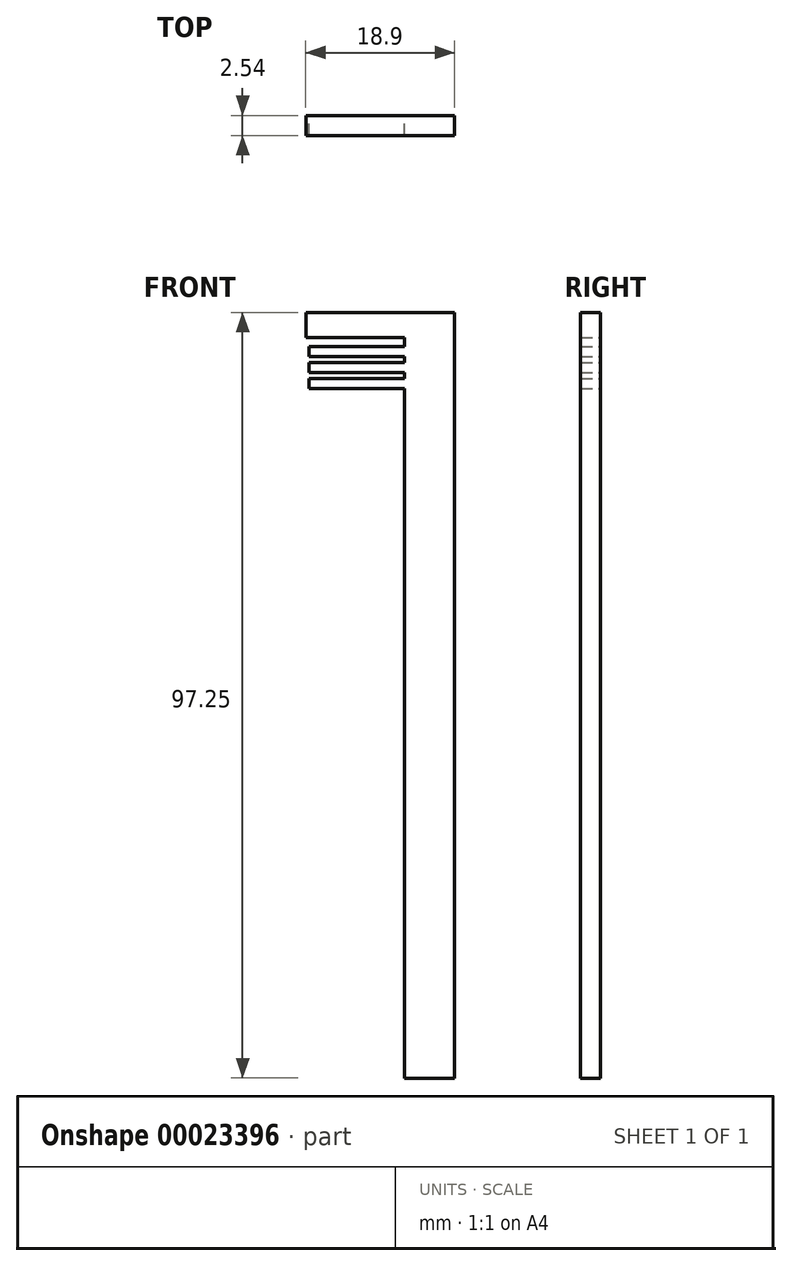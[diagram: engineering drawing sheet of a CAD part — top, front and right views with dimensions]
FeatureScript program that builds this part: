
annotation { "Feature Type Name" : "Feature", "Feature Type Description" : "" }
export const myFeature = defineFeature(function(context is Context, id is Id, definition is map)
    precondition{}
    {
        {
            var Q0;
            Q0=qCreatedBy(makeId("Front.planeOp"),FACE);
            var sketch = newSketch(context, id + "F0", { "sketchPlane" : qUnion([Q0])});
            skLineSegment(sketch, "E0.top", {"start": v(-6.35, 54.6) * mm, "end": v(-18.9, 54.6) * mm});
            skLineSegment(sketch, "E0.right", {"start": v(-18.9, 57.8) * mm, "end": v(-18.9, 54.6) * mm});
            skLineSegment(sketch, "E1", {"start": v(-6.35, 54.6) * mm, "end": v(-6.35, 53.45) * mm});
            skLineSegment(sketch, "E2", {"start": v(-6.35, -39.46) * mm, "end": v(0, -39.46) * mm});
            skLineSegment(sketch, "E3", {"start": v(0, 57.8) * mm, "end": v(0, -39.46) * mm});
            skLineSegment(sketch, "E4", {"start": v(-6.35, 53.45) * mm, "end": v(-18.48, 53.45) * mm});
            skLineSegment(sketch, "E5", {"start": v(-18.48, 53.45) * mm, "end": v(-18.48, 52.18) * mm});
            skLineSegment(sketch, "E6", {"start": v(-18.48, 52.18) * mm, "end": v(-6.35, 52.18) * mm});
            skLineSegment(sketch, "E7", {"start": v(-18.9, 57.8) * mm, "end": v(0, 57.8) * mm});
            skPoint(sketch, "E8.orphan", {"position": v(-18.9, 60.98) * mm});
            skLineSegment(sketch, "E9", {"start": v(-6.35, 51.42) * mm, "end": v(-18.48, 51.42) * mm});
            skLineSegment(sketch, "E10", {"start": v(-18.48, 51.42) * mm, "end": v(-18.48, 50.15) * mm});
            skLineSegment(sketch, "E11", {"start": v(-18.48, 50.15) * mm, "end": v(-6.35, 50.15) * mm});
            skLineSegment(sketch, "E12", {"start": v(-6.35, 49.39) * mm, "end": v(-18.48, 49.39) * mm});
            skLineSegment(sketch, "E13", {"start": v(-18.48, 49.39) * mm, "end": v(-18.48, 48.12) * mm});
            skLineSegment(sketch, "E14", {"start": v(-18.48, 48.12) * mm, "end": v(-6.35, 48.12) * mm});
            skLineSegment(sketch, "E15.trimOffspring", {"start": v(-6.35, 50.15) * mm, "end": v(-6.35, 49.39) * mm});
            skLineSegment(sketch, "E16.trimOffspring", {"start": v(-6.35, 48.12) * mm, "end": v(-6.35, -39.46) * mm});
            skLineSegment(sketch, "E17", {"start": v(-6.35, 52.18) * mm, "end": v(-6.35, 51.42) * mm});
            skLineSegment(sketch, "E18", {"start": v(-6.35, 48.12) * mm, "end": v(-6.35, 47.36) * mm});
            skLineSegment(sketch, "E19", {"start": v(-6.35, 47.36) * mm, "end": v(-6.35, 46.09) * mm});
            skLineSegment(sketch, "E20", {"start": v(-6.35, 46.09) * mm, "end": v(-6.35, 45.32) * mm});
            skLineSegment(sketch, "E21", {"start": v(-6.35, 45.32) * mm, "end": v(-6.35, 44.05) * mm});
            skLineSegment(sketch, "E22", {"start": v(-6.35, 44.05) * mm, "end": v(-6.35, 43.3) * mm});
            skLineSegment(sketch, "E23", {"start": v(-6.35, 43.3) * mm, "end": v(-6.35, 42.02) * mm});
            skLineSegment(sketch, "E24", {"start": v(-6.35, 42.02) * mm, "end": v(-6.35, 41.26) * mm});
            skLineSegment(sketch, "E25", {"start": v(-6.35, 41.26) * mm, "end": v(-6.35, 39.99) * mm});
            skLineSegment(sketch, "E26", {"start": v(-6.35, 39.99) * mm, "end": v(-6.35, 39.23) * mm});
            skLineSegment(sketch, "E27", {"start": v(-6.35, 39.23) * mm, "end": v(-6.35, 37.96) * mm});
            skLineSegment(sketch, "E28", {"start": v(-6.35, 37.96) * mm, "end": v(-6.35, 37.2) * mm});
            skLineSegment(sketch, "E29", {"start": v(-6.35, 37.2) * mm, "end": v(-6.35, 35.93) * mm});
            skLineSegment(sketch, "E30", {"start": v(-6.35, 35.93) * mm, "end": v(-6.35, 35.16) * mm});
            skLineSegment(sketch, "E31", {"start": v(-6.35, 35.16) * mm, "end": v(-6.35, 33.9) * mm});
            skLineSegment(sketch, "E32", {"start": v(-6.35, 33.9) * mm, "end": v(-6.35, 33.13) * mm});
            skLineSegment(sketch, "E33", {"start": v(-6.35, 33.13) * mm, "end": v(-6.35, 31.86) * mm});
            skLineSegment(sketch, "E34", {"start": v(-6.35, 31.86) * mm, "end": v(-6.35, 31.1) * mm});
            skLineSegment(sketch, "E35", {"start": v(-6.35, 31.1) * mm, "end": v(-6.35, 29.83) * mm});
            skLineSegment(sketch, "E36", {"start": v(-6.35, 29.83) * mm, "end": v(-6.35, 29.07) * mm});
            skLineSegment(sketch, "E37", {"start": v(-6.35, 29.07) * mm, "end": v(-6.35, 27.8) * mm});
            skLineSegment(sketch, "E38", {"start": v(-6.35, 27.8) * mm, "end": v(-6.35, 27.04) * mm});
            skLineSegment(sketch, "E39", {"start": v(-6.35, 47.36) * mm, "end": v(-18.48, 47.36) * mm});
            skLineSegment(sketch, "E40", {"start": v(-18.48, 47.36) * mm, "end": v(-18.48, 46.09) * mm});
            skLineSegment(sketch, "E41", {"start": v(-18.48, 46.09) * mm, "end": v(-6.35, 46.09) * mm});
            skLineSegment(sketch, "E42", {"start": v(-6.35, 45.32) * mm, "end": v(-18.48, 45.32) * mm});
            skLineSegment(sketch, "E43", {"start": v(-18.48, 45.32) * mm, "end": v(-18.48, 44.05) * mm});
            skLineSegment(sketch, "E44", {"start": v(-18.48, 44.05) * mm, "end": v(-6.35, 44.05) * mm});
            skLineSegment(sketch, "E45", {"start": v(-6.35, 43.3) * mm, "end": v(-18.48, 43.3) * mm});
            skLineSegment(sketch, "E46", {"start": v(-18.48, 43.3) * mm, "end": v(-18.48, 42.02) * mm});
            skLineSegment(sketch, "E47", {"start": v(-18.48, 42.02) * mm, "end": v(-6.35, 42.02) * mm});
            skLineSegment(sketch, "E48", {"start": v(-6.35, 41.26) * mm, "end": v(-18.48, 41.26) * mm});
            skLineSegment(sketch, "E49", {"start": v(-18.48, 41.26) * mm, "end": v(-18.48, 39.99) * mm});
            skLineSegment(sketch, "E50", {"start": v(-18.48, 39.99) * mm, "end": v(-6.35, 39.99) * mm});
            skLineSegment(sketch, "E51", {"start": v(-6.35, 39.23) * mm, "end": v(-18.48, 39.23) * mm});
            skLineSegment(sketch, "E52", {"start": v(-18.48, 39.23) * mm, "end": v(-18.48, 37.96) * mm});
            skLineSegment(sketch, "E53", {"start": v(-18.48, 37.96) * mm, "end": v(-6.35, 37.96) * mm});
            skLineSegment(sketch, "E54", {"start": v(-6.35, 37.2) * mm, "end": v(-18.48, 37.2) * mm});
            skLineSegment(sketch, "E55", {"start": v(-18.48, 37.2) * mm, "end": v(-18.48, 35.93) * mm});
            skLineSegment(sketch, "E56", {"start": v(-18.48, 35.93) * mm, "end": v(-6.35, 35.93) * mm});
            skLineSegment(sketch, "E57", {"start": v(-18.48, 35.16) * mm, "end": v(-6.35, 35.16) * mm});
            skLineSegment(sketch, "E58", {"start": v(-6.35, 33.9) * mm, "end": v(-18.48, 33.9) * mm});
            skLineSegment(sketch, "E59", {"start": v(-18.48, 33.9) * mm, "end": v(-18.48, 35.16) * mm});
            skLineSegment(sketch, "E60", {"start": v(-6.35, 33.13) * mm, "end": v(-18.48, 33.13) * mm});
            skLineSegment(sketch, "E61", {"start": v(-18.48, 33.13) * mm, "end": v(-18.48, 31.86) * mm});
            skLineSegment(sketch, "E62", {"start": v(-18.48, 31.86) * mm, "end": v(-6.35, 31.86) * mm});
            skLineSegment(sketch, "E63", {"start": v(-6.35, 31.1) * mm, "end": v(-18.48, 31.1) * mm});
            skLineSegment(sketch, "E64", {"start": v(-18.48, 31.1) * mm, "end": v(-18.48, 29.83) * mm});
            skLineSegment(sketch, "E65", {"start": v(-18.48, 29.83) * mm, "end": v(-6.35, 29.83) * mm});
            skLineSegment(sketch, "E66", {"start": v(-6.35, 29.07) * mm, "end": v(-18.48, 29.07) * mm});
            skLineSegment(sketch, "E67", {"start": v(-18.48, 29.07) * mm, "end": v(-18.48, 27.8) * mm});
            skLineSegment(sketch, "E68", {"start": v(-18.48, 27.8) * mm, "end": v(-6.35, 27.8) * mm});
            skLineSegment(sketch, "E69", {"start": v(-6.35, 27.04) * mm, "end": v(-6.35, 25.77) * mm});
            skLineSegment(sketch, "E70", {"start": v(-6.35, 25.77) * mm, "end": v(-6.35, 25) * mm});
            skLineSegment(sketch, "E71", {"start": v(-6.35, 25) * mm, "end": v(-6.35, 23.73) * mm});
            skLineSegment(sketch, "E72", {"start": v(-6.35, 24.25) * mm, "end": v(-6.35, 23.73) * mm});
            skLineSegment(sketch, "E73", {"start": v(-6.35, 24.25) * mm, "end": v(-6.35, 22.97) * mm});
            skLineSegment(sketch, "E74", {"start": v(-6.35, 22.97) * mm, "end": v(-6.35, 21.7) * mm});
            skLineSegment(sketch, "E75", {"start": v(-6.35, 21.8) * mm, "end": v(-6.35, 21.7) * mm});
            skLineSegment(sketch, "E76", {"start": v(-6.35, 21.8) * mm, "end": v(-6.35, 20.94) * mm});
            skLineSegment(sketch, "E77", {"start": v(-6.35, 20.94) * mm, "end": v(-6.35, 19.67) * mm});
            skLineSegment(sketch, "E78", {"start": v(-6.35, 19.67) * mm, "end": v(-6.35, 18.9) * mm});
            skLineSegment(sketch, "E79", {"start": v(-6.35, 18.9) * mm, "end": v(-6.35, 17.64) * mm});
            skLineSegment(sketch, "E80", {"start": v(-6.35, 17.64) * mm, "end": v(-6.35, 16.88) * mm});
            skLineSegment(sketch, "E81", {"start": v(-6.35, 16.88) * mm, "end": v(-6.35, 15.6) * mm});
            skLineSegment(sketch, "E82", {"start": v(-6.35, 15.6) * mm, "end": v(-6.35, 14.84) * mm});
            skLineSegment(sketch, "E83", {"start": v(-6.35, 14.84) * mm, "end": v(-6.35, 13.57) * mm});
            skLineSegment(sketch, "E84", {"start": v(-6.35, 13.57) * mm, "end": v(-6.35, 12.81) * mm});
            skLineSegment(sketch, "E85", {"start": v(-6.35, 12.81) * mm, "end": v(-6.35, 10.85) * mm});
            skLineSegment(sketch, "E86", {"start": v(-6.35, 10.85) * mm, "end": v(-6.35, 9.73) * mm});
            skLineSegment(sketch, "E87", {"start": v(-6.35, 9.73) * mm, "end": v(-6.35, 8.79) * mm});
            skLineSegment(sketch, "E88", {"start": v(-6.35, 8.79) * mm, "end": v(-6.35, 7.94) * mm});
            skLineSegment(sketch, "E89", {"start": v(-6.35, 7.94) * mm, "end": v(-6.35, 6.92) * mm});
            skLineSegment(sketch, "E90", {"start": v(-6.35, 6.92) * mm, "end": v(-6.35, 5.67) * mm});
            skLineSegment(sketch, "E91", {"start": v(-6.35, 5.67) * mm, "end": v(-6.35, 4.33) * mm});
            skLineSegment(sketch, "E92", {"start": v(-6.35, 4.33) * mm, "end": v(-6.35, 2.9) * mm});
            skLineSegment(sketch, "E93", {"start": v(-6.35, 2.9) * mm, "end": v(-6.35, 1.65) * mm});
            skLineSegment(sketch, "E94", {"start": v(-6.35, 1.65) * mm, "end": v(-6.35, 0.58) * mm});
            skLineSegment(sketch, "E95", {"start": v(-6.35, 0.58) * mm, "end": v(-6.35, -0.67) * mm});
            skLineSegment(sketch, "E96", {"start": v(-6.35, -0.67) * mm, "end": v(-6.35, -1.91) * mm});
            skLineSegment(sketch, "E97", {"start": v(-6.35, -1.91) * mm, "end": v(-6.35, -3.38) * mm});
            skLineSegment(sketch, "E98", {"start": v(-6.35, -3.38) * mm, "end": v(-6.35, -4.85) * mm});
            skLineSegment(sketch, "E99", {"start": v(-6.35, -4.85) * mm, "end": v(-6.35, -5.53) * mm});
            skLineSegment(sketch, "E100", {"start": v(-6.35, -5.53) * mm, "end": v(-6.35, -7.36) * mm});
            skLineSegment(sketch, "E101", {"start": v(-6.35, -7.36) * mm, "end": v(-6.35, -11.3) * mm});
            skLineSegment(sketch, "E102", {"start": v(-6.35, -11.3) * mm, "end": v(-6.35, -12.58) * mm});
            skLineSegment(sketch, "E103", {"start": v(-6.35, 27.04) * mm, "end": v(-18.48, 27.04) * mm});
            skLineSegment(sketch, "E104", {"start": v(-6.35, 25.77) * mm, "end": v(-18.48, 25.77) * mm});
            skLineSegment(sketch, "E105", {"start": v(-6.35, 25) * mm, "end": v(-18.48, 25) * mm});
            skLineSegment(sketch, "E106", {"start": v(-6.35, 23.73) * mm, "end": v(-18.48, 23.73) * mm});
            skLineSegment(sketch, "E107", {"start": v(-18.48, 23.73) * mm, "end": v(-18.48, 25) * mm});
            skLineSegment(sketch, "E108", {"start": v(-18.48, 27.04) * mm, "end": v(-18.48, 25.77) * mm});
            skLineSegment(sketch, "E109", {"start": v(-6.35, 22.97) * mm, "end": v(-18.48, 22.97) * mm});
            skLineSegment(sketch, "E110", {"start": v(-18.48, 22.97) * mm, "end": v(-18.48, 21.7) * mm});
            skLineSegment(sketch, "E111", {"start": v(-18.48, 21.7) * mm, "end": v(-6.35, 21.7) * mm});
            skSolve(sketch);
        }
        {
            var Q0;
            Q0=makeQuery(id+"F0.imprint","IMPRINT",FACE,{"disambiguationData":[TD([[makeQuery(id+"F0.imprint","IMPRINT",EDGE,{"derivedFrom":sQuery(id+"F0.wireOp",EDGE,"E0.bottom")}),1.0]])]});
            var Q1;
            Q1=makeQuery(id+"F0.imprint","IMPRINT",FACE,{"disambiguationData":[TD([[makeQuery(id+"F0.imprint","IMPRINT",EDGE,{"derivedFrom":sQuery(id+"F0.wireOp",EDGE,"E1")}),1.0]])]});
            var Q2;
            Q2=makeQuery(id+"F0.imprint","IMPRINT",FACE,{"disambiguationData":[TD([[makeQuery(id+"F0.imprint","IMPRINT",EDGE,{"derivedFrom":sQuery(id+"F0.wireOp",EDGE,"d43cbd1f-0e80-4fb0-a70e-29625bff22f6")}),-1.0]])]});
            var Q3;
            {var subQ1=sQuery(id+"F0.wireOp",EDGE,"E9");Q3=makeQuery(id+"F0.imprint","IMPRINT",FACE,{"disambiguationData":[TD([[makeQuery(id+"F0.imprint","IMPRINT",EDGE,{"derivedFrom":subQ1}),1.0]])]});}
            var Q4;
            {var subQ1=sQuery(id+"F0.wireOp",EDGE,"E12");Q4=makeQuery(id+"F0.imprint","IMPRINT",FACE,{"disambiguationData":[TD([[makeQuery(id+"F0.imprint","IMPRINT",EDGE,{"derivedFrom":subQ1}),1.0]])]});}
            var Q5;
            Q5=makeQuery(id+"F0.imprint","IMPRINT",FACE,{"disambiguationData":[TD([[makeQuery(id+"F0.imprint","IMPRINT",EDGE,{"derivedFrom":sQuery(id+"F0.wireOp",EDGE,"E19")}),-1.0]])]});
            var Q6;
            Q6=makeQuery(id+"F0.imprint","IMPRINT",FACE,{"disambiguationData":[TD([[makeQuery(id+"F0.imprint","IMPRINT",EDGE,{"derivedFrom":sQuery(id+"F0.wireOp",EDGE,"E21")}),-1.0]])]});
            var Q7;
            Q7=makeQuery(id+"F0.imprint","IMPRINT",FACE,{"disambiguationData":[TD([[makeQuery(id+"F0.imprint","IMPRINT",EDGE,{"derivedFrom":sQuery(id+"F0.wireOp",EDGE,"E23")}),-1.0]])]});
            var Q8;
            Q8=makeQuery(id+"F0.imprint","IMPRINT",FACE,{"disambiguationData":[TD([[makeQuery(id+"F0.imprint","IMPRINT",EDGE,{"derivedFrom":sQuery(id+"F0.wireOp",EDGE,"E25")}),-1.0]])]});
            var Q9;
            Q9=makeQuery(id+"F0.imprint","IMPRINT",FACE,{"disambiguationData":[TD([[makeQuery(id+"F0.imprint","IMPRINT",EDGE,{"derivedFrom":sQuery(id+"F0.wireOp",EDGE,"E27")}),-1.0]])]});
            var Q10;
            Q10=makeQuery(id+"F0.imprint","IMPRINT",FACE,{"disambiguationData":[TD([[makeQuery(id+"F0.imprint","IMPRINT",EDGE,{"derivedFrom":sQuery(id+"F0.wireOp",EDGE,"E29")}),-1.0]])]});
            var Q11;
            Q11=makeQuery(id+"F0.imprint","IMPRINT",FACE,{"disambiguationData":[TD([[makeQuery(id+"F0.imprint","IMPRINT",EDGE,{"derivedFrom":sQuery(id+"F0.wireOp",EDGE,"E31")}),-1.0]])]});
            var Q12;
            Q12=makeQuery(id+"F0.imprint","IMPRINT",FACE,{"disambiguationData":[TD([[makeQuery(id+"F0.imprint","IMPRINT",EDGE,{"derivedFrom":sQuery(id+"F0.wireOp",EDGE,"E33")}),-1.0]])]});
            var Q13;
            Q13=makeQuery(id+"F0.imprint","IMPRINT",FACE,{"disambiguationData":[TD([[makeQuery(id+"F0.imprint","IMPRINT",EDGE,{"derivedFrom":sQuery(id+"F0.wireOp",EDGE,"E35")}),-1.0]])]});
            var Q14;
            Q14=makeQuery(id+"F0.imprint","IMPRINT",FACE,{"disambiguationData":[TD([[makeQuery(id+"F0.imprint","IMPRINT",EDGE,{"derivedFrom":sQuery(id+"F0.wireOp",EDGE,"E37")}),-1.0]])]});
            extrude(context, id + "F1", {"entities" : qUnion([Q0, Q1, Q2, Q3, Q4, Q5, Q6, Q7, Q8, Q9, Q10, Q11, Q12, Q13, Q14]), "depth" : 2.54 * mm});
        }
    });
